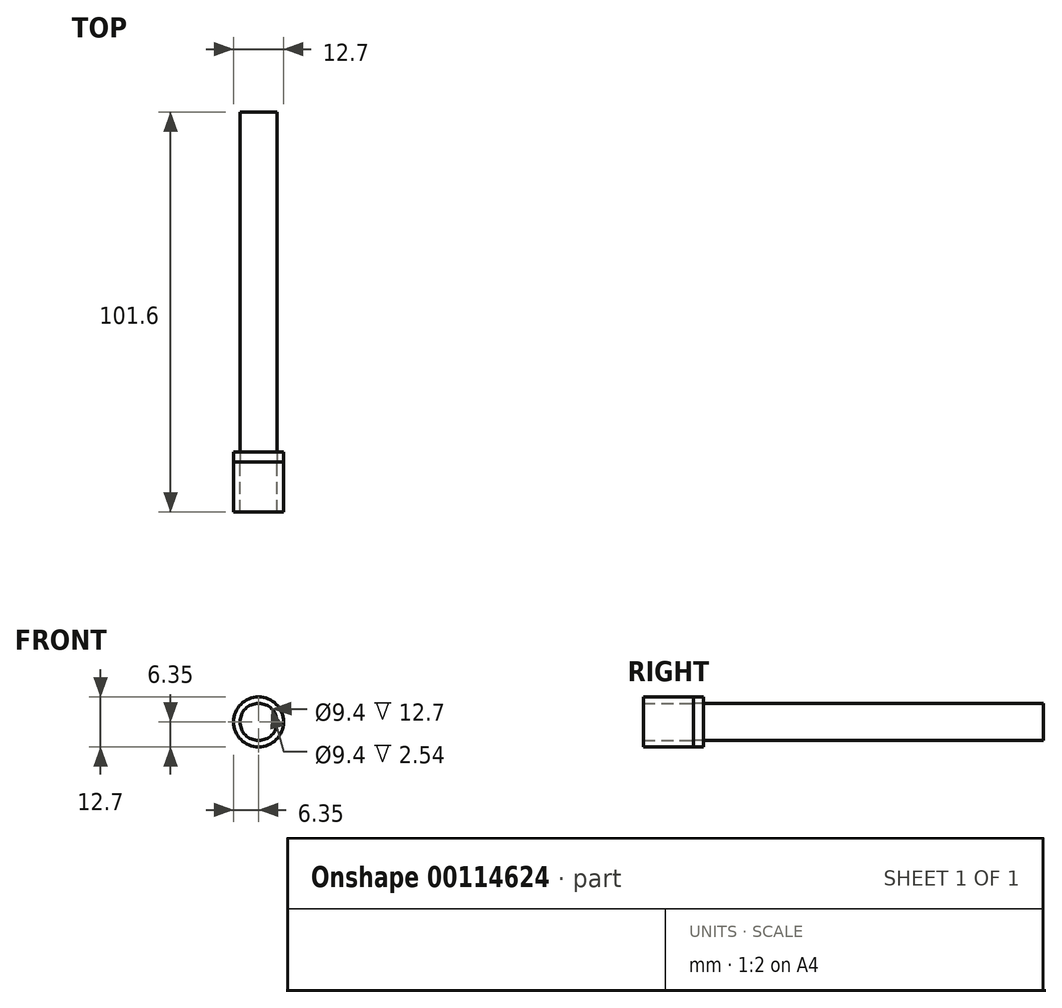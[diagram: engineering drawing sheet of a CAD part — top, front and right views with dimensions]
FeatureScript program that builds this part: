
annotation { "Feature Type Name" : "Feature", "Feature Type Description" : "" }
export const myFeature = defineFeature(function(context is Context, id is Id, definition is map)
    precondition{}
    {
        {
            var Q0;
            Q0=qCreatedBy(makeId("Front.planeOp"),FACE);
            var sketch = newSketch(context, id + "F0", { "sketchPlane" : qUnion([Q0])});
            skCircle(sketch, "E0", {"center": v(0, 0) * mm, "radius": 4.7 * mm});
            skSolve(sketch);
        }
        {
            var Q0;
            Q0=makeQuery(id+"F0.imprint","IMPRINT",FACE,{"disambiguationData":[TD([[makeQuery(id+"F0.imprint","IMPRINT",EDGE,{"derivedFrom":sQuery(id+"F0.wireOp",EDGE,"E0")}),1.0]])]});
            extrude(context, id + "F1", {"entities" : qUnion([Q0]), "depth" : 88.9 * mm});
        }
        {
            var Q0;
            Q0=makeQuery(id+"F1.opExtrude","CAP_FACE",FACE,{"disambiguationData":[OSD([sQuery(id+"F0.wireOp",EDGE,"E0")])],"isStart":false});
            var sketch = newSketch(context, id + "F2", { "sketchPlane" : qUnion([Q0])});
            skCircle(sketch, "E1", {"center": v(0, 0) * mm, "radius": 6.35 * mm});
            skSolve(sketch);
        }
        {
            var Q0;
            Q0=makeQuery(id+"F2.imprint","IMPRINT",FACE,{"disambiguationData":[TD([[makeQuery(id+"F2.imprint","IMPRINT",EDGE,{"derivedFrom":sQuery(id+"F2.wireOp",EDGE,"E1")}),1.0]])]});
            extrude(context, id + "F3", {"entities" : qUnion([Q0]), "depth" : 12.7 * mm});
        }
        {
            var Q0;
            Q0=makeQuery(id+"F3.opExtrude","CAP_FACE",FACE,{"disambiguationData":[OSD([sQuery(id+"F0.wireOp",EDGE,"E0"),sQuery(id+"F2.wireOp",EDGE,"E1")])],"isStart":true});
            extrude(context, id + "F4", {"entities" : qUnion([Q0]), "depth" : 2.54 * mm});
        }
    });
